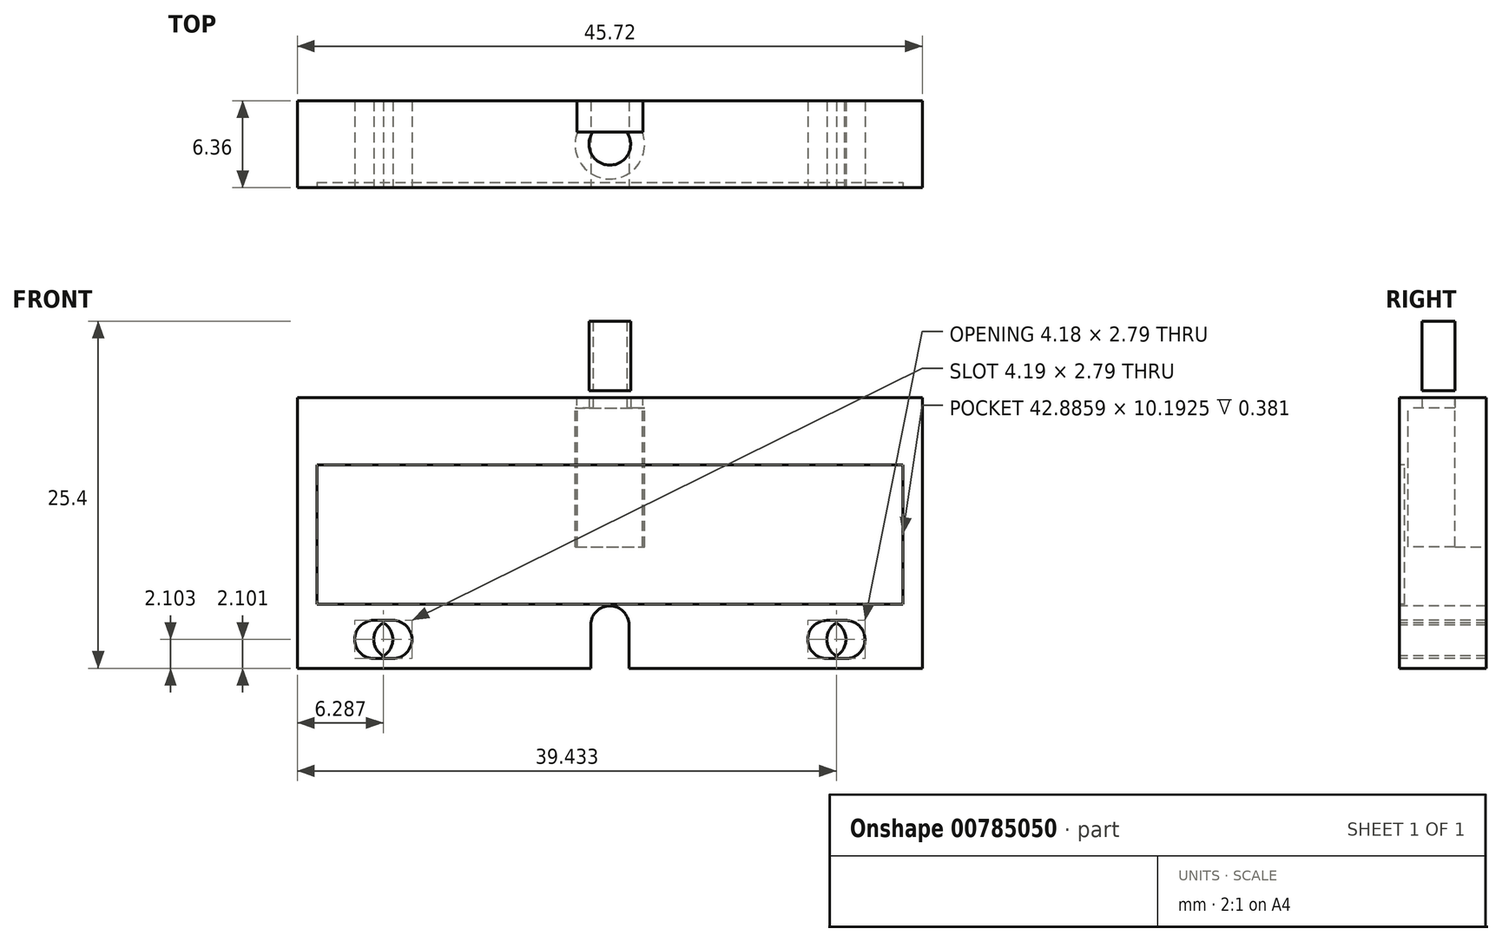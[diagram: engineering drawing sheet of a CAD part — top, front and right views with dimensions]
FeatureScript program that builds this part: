
annotation { "Feature Type Name" : "Feature", "Feature Type Description" : "" }
export const myFeature = defineFeature(function(context is Context, id is Id, definition is map)
    precondition{}
    {
        {
            var Q0;
            Q0=qCreatedBy(makeId("Top.planeOp"),FACE);
            var sketch = newSketch(context, id + "F0", { "sketchPlane" : qUnion([Q0])});
            skCircle(sketch, "E0", {"center": v(0, 0) * mm, "radius": 1.52 * mm});
            skSolve(sketch);
        }
        {
            var Q0;
            Q0=qCreatedBy(makeId("Top.planeOp"),FACE);
            var sketch = newSketch(context, id + "F1", { "sketchPlane" : qUnion([Q0])});
            skCircle(sketch, "E1", {"center": v(0, 0) * mm, "radius": 2.54 * mm});
            skSolve(sketch);
        }
        {
            var Q0;
            Q0 = qSketchRegion(id + "F0", true);
            extrude(context, id + "F2", {"entities" : qUnion([Q0]), "depth" : 6.35 * mm, "offsetDistance" : 25.4 * mm});
        }
        {
            var Q0;
            Q0 = qSketchRegion(id + "F1", true);
            extrude(context, id + "F3", {"entities" : qUnion([Q0]), "operationType" : NewBodyOperationType.ADD, "oppositeDirection" : true, "depth" : 10.16 * mm, "offsetDistance" : 25.4 * mm});
        }
        {
            var Q0;
            Q0=qCreatedBy(makeId("Top.planeOp"),FACE);
            var sketch = newSketch(context, id + "F4", { "sketchPlane" : qUnion([Q0])});
            skLineSegment(sketch, "E2.bottom", {"start": v(22.86, -3.17) * mm, "end": v(-22.86, -3.18) * mm});
            skLineSegment(sketch, "E2.top", {"start": v(22.86, 3.18) * mm, "end": v(-22.86, 3.17) * mm});
            skLineSegment(sketch, "E2.left", {"start": v(22.86, -3.17) * mm, "end": v(22.86, 3.18) * mm});
            skLineSegment(sketch, "E2.right", {"start": v(-22.86, -3.18) * mm, "end": v(-22.86, 3.17) * mm});
            skPoint(sketch, "E2.middle", {"position": v(0, 0) * mm});
            skSolve(sketch);
        }
        {
            var Q0;
            Q0 = qSketchRegion(id + "F4", true);
            extrude(context, id + "F5", {"entities" : qUnion([Q0]), "oppositeDirection" : true, "depth" : 13.97 * mm, "offsetDistance" : 25.4 * mm});
        }
        {
            var Q0;
            Q0=makeQuery(id+"F5.opExtrude","CAP_FACE",FACE,{"disambiguationData":[OSD([sQuery(id+"F4.wireOp",EDGE,"E2.bottom"),sQuery(id+"F4.wireOp",EDGE,"E2.top"),sQuery(id+"F4.wireOp",EDGE,"E2.left"),sQuery(id+"F4.wireOp",EDGE,"E2.right")])],"isStart":true});
            extrude(context, id + "F6", {"entities" : qUnion([Q0]), "operationType" : NewBodyOperationType.ADD, "depth" : 0.76 * mm, "offsetDistance" : 25.4 * mm});
        }
        {
            var Q0;
            Q0 = qSketchRegion(id + "F1", true);
            extrude(context, id + "F7", {"entities" : qUnion([Q0]), "operationType" : NewBodyOperationType.REMOVE, "oppositeDirection" : true, "depth" : 10.16 * mm, "offsetDistance" : 25.4 * mm});
        }
        {
            var Q0;
            Q0 = qSketchRegion(id + "F0", true);
            extrude(context, id + "F8", {"entities" : qUnion([Q0]), "operationType" : NewBodyOperationType.REMOVE, "depth" : 1.27 * mm, "offsetDistance" : 25.4 * mm});
        }
        {
            var Q0;
            Q0=makeQuery(id+"F5.opExtrude","CAP_FACE",FACE,{"disambiguationData":[OSD([sQuery(id+"F4.wireOp",EDGE,"E2.bottom"),sQuery(id+"F4.wireOp",EDGE,"E2.top"),sQuery(id+"F4.wireOp",EDGE,"E2.left"),sQuery(id+"F4.wireOp",EDGE,"E2.right")])],"isStart":false});
            extrude(context, id + "F9", {"entities" : qUnion([Q0]), "operationType" : NewBodyOperationType.ADD, "depth" : 5.08 * mm, "offsetDistance" : 25.4 * mm});
        }
        {
            var Q0;
            {var subQ0=sQuery(id+"F4.wireOp",EDGE,"E2.bottom");Q0=makeQuery(id+"F9.boolean.opBoolean","MERGE",FACE,{"derivedFrom":[makeQuery(id+"F6.boolean.opBoolean","MERGE",FACE,{"derivedFrom":[makeQuery(id+"F5.opExtrude","SWEPT_FACE",FACE,{"disambiguationData":[OSD([subQ0])]}),makeQuery(id+"F6.opExtrude","SWEPT_FACE",FACE,{"disambiguationData":[OSD([subQ0])]})]}),makeQuery(id+"F9.opExtrude","SWEPT_FACE",FACE,{"disambiguationData":[OSD([subQ0])]})]});}
            var sketch = newSketch(context, id + "F10", { "sketchPlane" : qUnion([Q0])});
            skCircle(sketch, "E3", {"center": v(-15.88, -16.95) * mm, "radius": 1.4 * mm});
            skCircle(sketch, "E4", {"center": v(15.88, -16.95) * mm, "radius": 1.4 * mm});
            skCircle(sketch, "E5", {"center": v(0, -15.88) * mm, "radius": 1.4 * mm});
            skLineSegment(sketch, "E6.bottom", {"start": v(-1.4, -15.88) * mm, "end": v(1.4, -15.88) * mm});
            skLineSegment(sketch, "E6.top", {"start": v(-1.4, -20.2) * mm, "end": v(1.4, -20.2) * mm});
            skLineSegment(sketch, "E6.left", {"start": v(-1.4, -15.88) * mm, "end": v(-1.4, -20.2) * mm});
            skLineSegment(sketch, "E6.right", {"start": v(1.4, -15.88) * mm, "end": v(1.4, -20.2) * mm});
            skCircle(sketch, "E7", {"center": v(-17.27, -16.95) * mm, "radius": 1.4 * mm});
            skCircle(sketch, "E8", {"center": v(17.27, -16.95) * mm, "radius": 1.4 * mm});
            skLineSegment(sketch, "E9.bottom", {"start": v(-17.27, -15.55) * mm, "end": v(-15.88, -15.55) * mm});
            skLineSegment(sketch, "E9.top", {"start": v(-17.27, -18.34) * mm, "end": v(-15.88, -18.34) * mm});
            skLineSegment(sketch, "E10.bottom", {"start": v(15.88, -15.55) * mm, "end": v(17.27, -15.55) * mm});
            skLineSegment(sketch, "E10.top", {"start": v(15.88, -18.34) * mm, "end": v(17.27, -18.34) * mm});
            skLineSegment(sketch, "E10.left", {"start": v(15.88, -15.55) * mm, "end": v(15.88, -18.34) * mm});
            skLineSegment(sketch, "E10.right", {"start": v(17.27, -15.55) * mm, "end": v(17.27, -18.34) * mm});
            skSolve(sketch);
        }
        {
            var Q0;
            Q0 = qSketchRegion(id + "F10", true);
            extrude(context, id + "F11", {"entities" : qUnion([Q0]), "operationType" : NewBodyOperationType.REMOVE, "oppositeDirection" : true, "depth" : 25.4 * mm, "offsetDistance" : 25.4 * mm});
        }
        {
            var Q0;
            {var subQ0=sQuery(id+"F4.wireOp",EDGE,"E2.bottom");Q0=makeQuery(id+"F9.boolean.opBoolean","MERGE",FACE,{"derivedFrom":[makeQuery(id+"F6.boolean.opBoolean","MERGE",FACE,{"derivedFrom":[makeQuery(id+"F5.opExtrude","SWEPT_FACE",FACE,{"disambiguationData":[OSD([subQ0])]}),makeQuery(id+"F6.opExtrude","SWEPT_FACE",FACE,{"disambiguationData":[OSD([subQ0])]})]}),makeQuery(id+"F9.opExtrude","SWEPT_FACE",FACE,{"disambiguationData":[OSD([subQ0])]})]});}
            var sketch = newSketch(context, id + "F12", { "sketchPlane" : qUnion([Q0])});
            skPoint(sketch, "E11.firstSnap0", {"position": v(0, -14.48) * mm});
            skLineSegment(sketch, "E11.bottom", {"start": v(0, -14.35) * mm, "end": v(21.45, -14.35) * mm});
            skLineSegment(sketch, "E11.top", {"start": v(0, -4.16) * mm, "end": v(21.45, -4.16) * mm});
            skLineSegment(sketch, "E11.left", {"start": v(0, -14.35) * mm, "end": v(0, -4.16) * mm});
            skLineSegment(sketch, "E11.right", {"start": v(21.45, -14.35) * mm, "end": v(21.45, -4.16) * mm});
            skLineSegment(sketch, "E12.bottom", {"start": v(0, -14.35) * mm, "end": v(-21.44, -14.35) * mm});
            skLineSegment(sketch, "E12.top", {"start": v(0, -4.16) * mm, "end": v(-21.44, -4.16) * mm});
            skLineSegment(sketch, "E12.right", {"start": v(-21.44, -14.35) * mm, "end": v(-21.44, -4.16) * mm});
            skSolve(sketch);
        }
        {
            var Q0;
            Q0 = qSketchRegion(id + "F12", true);
            extrude(context, id + "F13", {"entities" : qUnion([Q0]), "operationType" : NewBodyOperationType.REMOVE, "oppositeDirection" : true, "depth" : 0.38 * mm, "offsetDistance" : 25.4 * mm});
        }
        {
            var Q0;
            {var subQ0=sQuery(id+"F4.wireOp",EDGE,"E2.top");Q0=makeQuery(id+"F9.boolean.opBoolean","MERGE",FACE,{"derivedFrom":[makeQuery(id+"F6.boolean.opBoolean","MERGE",FACE,{"derivedFrom":[makeQuery(id+"F5.opExtrude","SWEPT_FACE",FACE,{"disambiguationData":[OSD([subQ0])]}),makeQuery(id+"F6.opExtrude","SWEPT_FACE",FACE,{"disambiguationData":[OSD([subQ0])]})]}),makeQuery(id+"F9.opExtrude","SWEPT_FACE",FACE,{"disambiguationData":[OSD([subQ0])]})]});}
            var sketch = newSketch(context, id + "F14", { "sketchPlane" : qUnion([Q0])});
            skLineSegment(sketch, "E13.bottom", {"start": v(2.41, -10.16) * mm, "end": v(-2.41, -10.16) * mm});
            skLineSegment(sketch, "E13.top", {"start": v(2.41, 10.16) * mm, "end": v(-2.41, 10.16) * mm});
            skLineSegment(sketch, "E13.left", {"start": v(2.41, -10.16) * mm, "end": v(2.41, 10.16) * mm});
            skLineSegment(sketch, "E13.right", {"start": v(-2.41, -10.16) * mm, "end": v(-2.41, 10.16) * mm});
            skPoint(sketch, "E13.middle", {"position": v(0, 0) * mm});
            skSolve(sketch);
        }
        {
            var Q0;
            Q0 = qSketchRegion(id + "F14", true);
            extrude(context, id + "F15", {"entities" : qUnion([Q0]), "operationType" : NewBodyOperationType.REMOVE, "oppositeDirection" : true, "depth" : 2.3 * mm, "offsetDistance" : 25.4 * mm});
        }
    });
